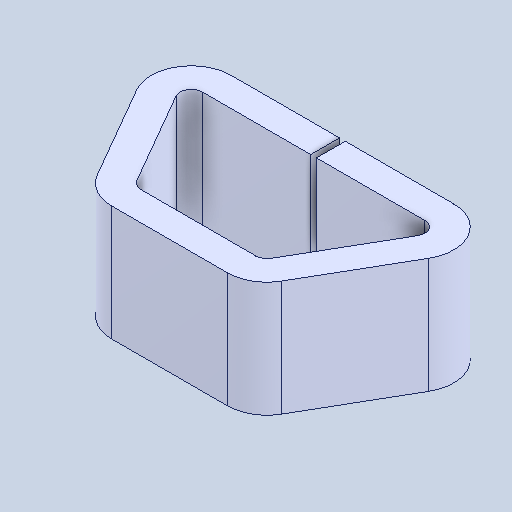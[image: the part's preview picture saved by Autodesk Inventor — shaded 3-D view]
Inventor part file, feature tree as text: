
AUTODESK INVENTOR PART (.ipt)
format: ipt  version: 2025 (Build 290162000, 162)  size: 107,520 bytes
history: native  units: mm
features: mirror x1
ambient origin geometry x8: Origin, YZ Plane, XZ Plane, XY Plane, X Axis, Y Axis, Z Axis, Center Point
bodies: Solid1 (feature_tree)
feature tree (1):
  mirror  "Mirror1"
